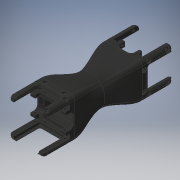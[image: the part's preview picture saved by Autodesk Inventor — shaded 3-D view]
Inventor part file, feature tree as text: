
AUTODESK INVENTOR PART (.ipt)
format: ipt  version: 2019 (Build 230136000, 136)  size: 1,923,584 bytes
history: native  units: mm
features: extrude x10, sketch x6, mirror x6, fillet x3, chamfer x2, thicken_offset x2, other x2, plane x1, loft x1, shell x1, move_body x1, projected_geometry x1
ambient origin geometry x8: Origin, YZ Plane, XZ Plane, XY Plane, X Axis, Y Axis, Z Axis, Center Point
bodies: Solid1 (feature_tree), Solid2 (feature_tree)
feature tree (36):
  sketch  "Sketch1"  dims[d0=35.0mm d1=3.0mm]
  plane  "Work Plane1"
  sketch  "Sketch2"  dims[d2=38.0mm d3=29.5mm]
  extrude  "Extrusion1"  Depth=3.0mm
  extrude  "Extrusion2"  Depth=29.5mm
  extrude  "Extrusion3"  Depth=25.0mm
  mirror  "Mirror2"
  sketch  "Sketch5"  dims[d11=5.6mm d12=2.0mm d13=5.6mm d14=0.0mm]
  mirror  "Mirror1"
  fillet  "Fillet1"  Radius=29.5mm
  loft  "Loft1"
  shell  "Shell1"  Thickness=17.25mm
  extrude  "Extrusion4"  Depth=2.0mm
  fillet  "Fillet2"  Radius=5.6mm
  extrude  "Extrusion5"  Depth=5.6mm TaperAngle=0.0deg
  extrude  "Extrusion9"  TaperAngle=90.0deg  [1 undecoded]
  extrude  "Extrusion10"  Depth=10.0mm
  chamfer  "Chamfer1"  Distance=10.0mm Angle=90.0deg
  chamfer  "Chamfer2"  Distance=2.5mm
  mirror  "Mirror3"
  extrude  "Extrusion6"  Depth=5.0mm
  extrude  "Extrusion7"  Depth=9.773844mm
  mirror  "Mirror4"
  mirror  "Mirror5"
  extrude  "Extrusion8"  Depth=5.6mm TaperAngle=0.0deg
  fillet  "Fillet3"  Radius=3.75mm
  mirror  "Mirror6"
  move_body  "Move Body1"
  thicken_offset  "Thicken1"
  thicken_offset  "Thicken2"
  sketch  "Sketch3"  dims[d4=41.5mm d5=25.0mm d6=29.5mm]
  other  "Edges1"
  sketch  "Sketch4"  dims[d7=36.0mm d8=0.0mm d9=5.6mm d10=17.25mm]
  sketch  "Sketch7"  dims[d15=4.0mm d17=5.6mm d18=0.0mm d20=90.0deg d23=10.0mm d24=10.0mm d25=90.0deg d26=2.5mm d27=5.0mm d28=9.773844mm d32=5.6mm d33=0.0mm d34=3.75mm d35=0.5mm d36=4.0mm d37=5.6mm d38=0.0mm d39=8.1mm d40=34.6mm d41=2.7mm d42=22.0mm d43=30.1mm d44=2.5mm d45=5.0mm d46=2.5mm d47=5.0mm d48=2.5mm d49=5.0mm d50=10.0mm d51=0.0mm d52=2.0mm d53=0.0mm d60=2.0mm d61=2.0mm d62=2.0mm d63=0.0mm d64=4.0mm d65=0.5mm d66=90.0deg d67=0.5mm d68=0.5mm d69=0.5mm d70=0.5mm d71=11.0mm d72=0.0mm d73=4.0mm d74=4.0mm d75=3.0mm d76=0.0mm d77=2.0mm d78=2.0mm d79=45.0deg d80=1.0mm d81=2.0mm d82=45.0deg d83=2.0mm d84=2.0mm d85=2.0mm]
  projected_geometry  "Projected Loop1"
  other  "Pattern of Solid1:1"
note: 1 required parameter value undecoded (feature->parameter linkage not recoverable at this tier; creation-order binding heuristic only, values carry confidence <= 0.55)
